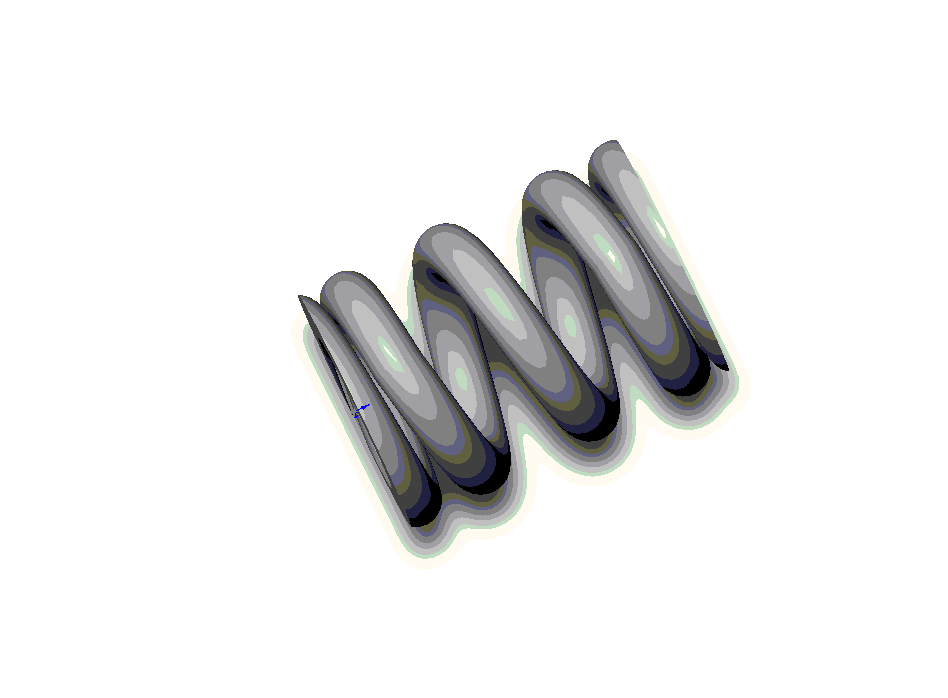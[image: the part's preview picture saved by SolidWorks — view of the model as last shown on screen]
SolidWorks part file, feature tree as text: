
SOLIDWORKS PART (.sldprt)
format: sldprt  version: not decoded by parser v0  size: 1,058,816 bytes
history: native  units: mm
features: plane x6, sketch x6, helix x3, material x1, sweep x1, cut_revolve x1 (+8 scaffold rows collapsed)
feature tree (26):
  scaffold x8  (default folders/planes/origin — collapsed)
  material  "Matériau <non spécifié>"
  plane  "Plan1"
  plane  "Plan2"
  plane  "Plan appui 1"
  sketch  "def2"  dims[c=1.05mm]
  plane  "départ hélice début"  Offset=7.875mm
  sketch  "def"  dims[d=15.0mm L=100.0mm de=10.0mm dm=60.0mm n=2.0mm c=1.2mm]
  sketch  "cercle début"
  plane  "départ hélice milieu"  Offset=15.75mm
  plane  "départ hélice fin"  Offset=84.25mm
  helix  "Hélice début"  Pitch=23.625mm p=15.75mm
  sketch  "cercle milieu"
  helix  "Hélice milieu"  Pitch=68.5mm H=68.5mm n=2
  sketch  "cercle fin"
  helix  "Hélice fin"  Pitch=23.625mm p=15.75mm n=1.5
  sweep  "Base-Balayage"
  sketch  "tronquage"  dims[D1=15.0mm D2=75.0mm]
  cut_revolve  "meulage extrémités"  Angle=360deg
decode coverage: 7 of 11 modeling features carry decoded parameters
note: suppression state not decoded; provenance and decode notes live in map.json
